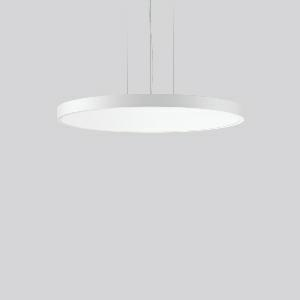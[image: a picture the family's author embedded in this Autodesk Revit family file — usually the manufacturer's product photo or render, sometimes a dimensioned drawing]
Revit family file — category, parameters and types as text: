
# Revit family: triona_round_p_312389_002_2_76_3074
name_source: partatom
category: Lighting Fixtures
units: mm (PartAtom-declared; Revit-internal decimal feet)

## family parameters
Cut with Voids When Loaded = No
Host = Face
Light Source = No
Part Type = Normal
Room Calculation Point = No
Round Connector Dimension = Use Diameter
Shared = No

## types (1)
- TuneableWhite 846 (1 x LED Modul 846, 4800 lm, 4600)
    Apparent Load = 49 VA
    CIE Flux Codes = 50 80 96 100 100
    Color Rendering = 80
    Color Temperature = 4600
    Default Elevation = 1800 mm
    Description = Series: TRIONA round
Decorative round LED pendant-mounted surface luminaire. Flat, seamless frame: aluminium extrusion profile, powder coated. Cover made of sheet steel, powder-coated. Canopy made of aluminium, powder-coated. Light emission through a diffuser: plastic, opal. Lightguide and diffuser made of non-yellowing plastic (PMMA). Lateral light emission (RZB SIDELITE technology) for above-average homogeneous light distribution. Tunable white versions, dynamically adjustable from 2700 K to 6500 K. 3-point steel cable suspension, steplessly adjustable. Easy installation with transparent, adjustable pendant cable and canopy with magnetic fixing. Driver integrated. Ideal for use as part of the Human Centric Lighting concept in connection with RZB light management systems. 
Colour: traffic white, matt (RAL 9016)
Diameter: 845 mm
Height: 52 mm
Suspension length: 500-1200 mm
Lamp: LED
Socket: without socket
Colour temperature: 2700K - 6500K
Colour rendering index (CRI): 80
System power: 49 W
Rated luminous flux: 4800 lm
Luminous efficiency: 98 lm/W
System power 2: 51 W
Rated luminous flux 2: 4550 lm
Luminous efficiency 2: 89 lm/W
System power 3: 51 W
Rated luminous flux 3: 4650 lm
Luminous efficiency 3: 91 lm/W
Control gear: Converter, dimmable, DALI
Protection class: I
Type of protection: IP 20
    Height = 52 mm  [stored 0.170604 ft]
    Lamp = 1 x LED Modul 846
    Lamp Light Flux = 4800 lm
    Lamp count = 1
    Length = 845 mm
    Lifetime = 50000 h
    Luminous efficacy = 98 lm/W
    Manufacturer = RZB
    ModVariant = No
    Model = 312389.002.2.76
    Mounting Place = Ceiling
    Mounting Type = Pendant
    Number of Poles = 1
    OnlyDefault = Yes
    Power Factor = 1
    Product Name = TRIONA round P
    Product group = Pendant modular luminaires
    ProductGroupID = 906
    Protection Class = Protection class I
    Protection Degree = IP 20
    RLX_Detail_Level = 1
    RLX_Emergency_Light_Flux = 0 lm
    RLX_Emergency_Type = 0
    RLX_Emergency_Type_DB = No
    RlxData = <blob elided: 29089 chars, md5=d0fa8467>
    Socket = socket
    Standby Power = 0 W
    System Light Flux = 4800 lm
    System Power = 49 W
    Type Comments = TuneableWhite 846
    Type Image = 312390.002.jpg
    URL = http://relux.com
    VarID = tuneablewhite_846
    Voltage = 230 V
    Voltage Range = 220-240 V
    Weight = 0.00 kg
    Width = 0 mm  [stored 0 ft]

note: [stored X ft] marks values corroborated as IEEE doubles in the binary element streams (Revit-internal decimal feet)

## geometry (parser evidence)
native form markers: Blend x4, Sweep x10
no freeform markers — native parametric forms only
